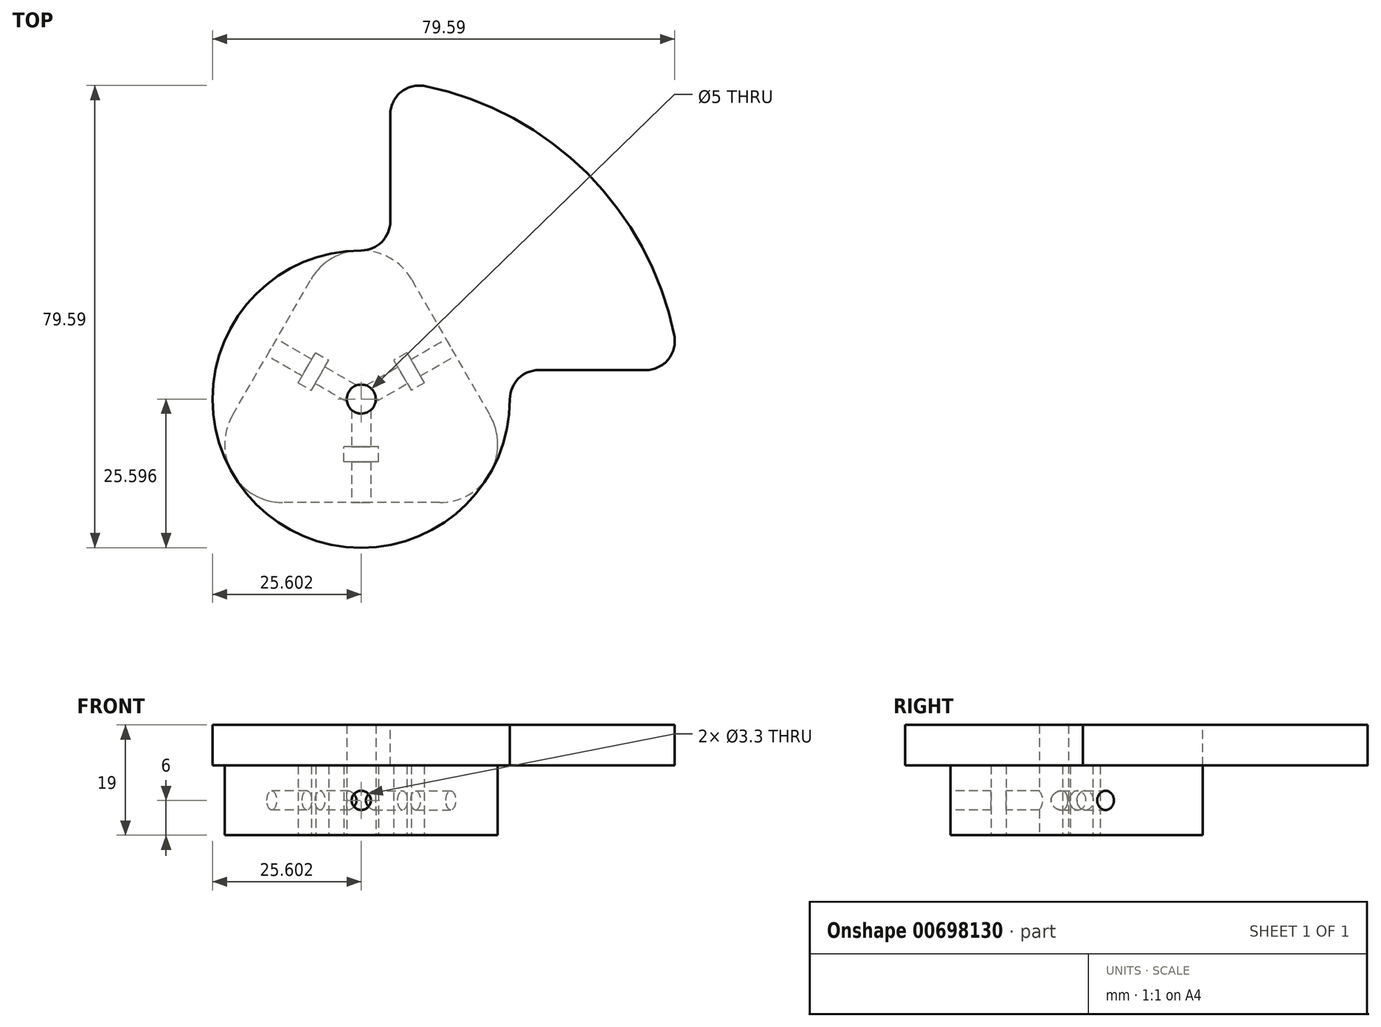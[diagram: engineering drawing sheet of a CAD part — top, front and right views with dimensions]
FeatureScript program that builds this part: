
annotation { "Feature Type Name" : "Feature", "Feature Type Description" : "" }
export const myFeature = defineFeature(function(context is Context, id is Id, definition is map)
    precondition{}
    {
        {
            var Q0;
            Q0=qCreatedBy(makeId("Top.planeOp"),FACE);
            var sketch = newSketch(context, id + "F0", { "sketchPlane" : qUnion([Q0])});
            skCircle(sketch, "E0.cCircle", {"center": v(-16.65, 9.96) * mm, "radius": 35.6 * mm, "construction": true});
            skLineSegment(sketch, "E0.0", {"start": v(14.18, -7.84) * mm, "end": v(-47.48, -7.84) * mm});
            skLineSegment(sketch, "E0.1", {"start": v(-47.48, -7.84) * mm, "end": v(-16.65, 45.56) * mm});
            skLineSegment(sketch, "E0.2", {"start": v(-16.65, 45.56) * mm, "end": v(14.18, -7.84) * mm});
            skCircle(sketch, "E1", {"center": v(-16.65, 9.96) * mm, "radius": 2.5 * mm});
            skPoint(sketch, "E2", {"position": v(-32.06, 18.86) * mm});
            skPoint(sketch, "E3", {"position": v(-1.23, 18.86) * mm});
            skPoint(sketch, "E4", {"position": v(-16.65, -7.84) * mm});
            skLineSegment(sketch, "E5", {"start": v(-32.06, 18.86) * mm, "end": v(-16.65, 9.96) * mm, "construction": true});
            skLineSegment(sketch, "E6", {"start": v(-16.65, -7.84) * mm, "end": v(-16.65, 9.96) * mm, "construction": true});
            skLineSegment(sketch, "E7", {"start": v(-16.65, 9.96) * mm, "end": v(-1.23, 18.86) * mm, "construction": true});
            skLineSegment(sketch, "E8.bottom", {"start": v(-13.65, -0.84) * mm, "end": v(-19.65, -0.84) * mm});
            skLineSegment(sketch, "E8.top", {"start": v(-13.65, 1.76) * mm, "end": v(-19.65, 1.76) * mm});
            skLineSegment(sketch, "E8.left", {"start": v(-13.65, -0.84) * mm, "end": v(-13.65, 1.76) * mm});
            skLineSegment(sketch, "E8.right", {"start": v(-19.65, -0.84) * mm, "end": v(-19.65, 1.76) * mm});
            skPoint(sketch, "E8.middle", {"position": v(-16.65, 0.46) * mm});
            skLineSegment(sketch, "E9.1.0", {"start": v(-8.8, 17.95) * mm, "end": v(-5.8, 12.76) * mm});
            skLineSegment(sketch, "E9.1.1", {"start": v(-11.05, 16.65) * mm, "end": v(-8.05, 11.46) * mm});
            skLineSegment(sketch, "E9.1.2", {"start": v(-8.8, 17.95) * mm, "end": v(-11.05, 16.65) * mm});
            skLineSegment(sketch, "E9.1.3", {"start": v(-5.8, 12.76) * mm, "end": v(-8.05, 11.46) * mm});
            skPoint(sketch, "E9.1.4", {"position": v(-8.42, 14.7) * mm});
            skLineSegment(sketch, "E9.2.0", {"start": v(-27.5, 12.76) * mm, "end": v(-24.5, 17.95) * mm});
            skLineSegment(sketch, "E9.2.1", {"start": v(-25.25, 11.46) * mm, "end": v(-22.25, 16.65) * mm});
            skLineSegment(sketch, "E9.2.2", {"start": v(-27.5, 12.76) * mm, "end": v(-25.25, 11.46) * mm});
            skLineSegment(sketch, "E9.2.3", {"start": v(-24.5, 17.95) * mm, "end": v(-22.25, 16.65) * mm});
            skPoint(sketch, "E9.2.4", {"position": v(-24.88, 14.7) * mm});
            skSolve(sketch);
        }
        {
            var Q0;
            Q0=makeQuery(id+"F0.imprint","IMPRINT",FACE,{"disambiguationData":[TD([[makeQuery(id+"F0.imprint","IMPRINT",EDGE,{"derivedFrom":sQuery(id+"F0.wireOp",EDGE,"E0.0")}),-1.0]])]});
            var Q1;
            Q1=makeQuery(id+"F0.imprint","IMPRINT",FACE,{"disambiguationData":[TD([[makeQuery(id+"F0.imprint","IMPRINT",EDGE,{"derivedFrom":sQuery(id+"F0.wireOp",EDGE,"E8.bottom")}),-1.0]])]});
            var Q2;
            Q2=makeQuery(id+"F0.imprint","IMPRINT",FACE,{"disambiguationData":[TD([[makeQuery(id+"F0.imprint","IMPRINT",EDGE,{"derivedFrom":sQuery(id+"F0.wireOp",EDGE,"E9.1.0")}),-1.0]])]});
            var Q3;
            Q3=makeQuery(id+"F0.imprint","IMPRINT",FACE,{"disambiguationData":[TD([[makeQuery(id+"F0.imprint","IMPRINT",EDGE,{"derivedFrom":sQuery(id+"F0.wireOp",EDGE,"E9.2.0")}),-1.0]])]});
            extrude(context, id + "F1", {"entities" : qUnion([Q0, Q1, Q2, Q3]), "depth" : 12 * mm, "offsetDistance" : 25 * mm});
        }
        {
            var Q0;
            Q0=makeQuery(id+"F1.opExtrude","SWEPT_EDGE",EDGE,{"disambiguationData":[OSD([sQuery(id+"F0.wireOp",EDGE,"E0.0"),sQuery(id+"F0.wireOp",EDGE,"E0.1")])]});
            var Q1;
            Q1=makeQuery(id+"F1.opExtrude","SWEPT_EDGE",EDGE,{"disambiguationData":[OSD([sQuery(id+"F0.wireOp",EDGE,"E0.0"),sQuery(id+"F0.wireOp",EDGE,"E0.2")])]});
            var Q2;
            Q2=makeQuery(id+"F1.opExtrude","SWEPT_EDGE",EDGE,{"disambiguationData":[OSD([sQuery(id+"F0.wireOp",EDGE,"E0.1"),sQuery(id+"F0.wireOp",EDGE,"E0.2")])]});
            fillet(context, id + "F2", {"entities" : qUnion([Q0, Q1, Q2]), "radius" : 10 * mm, "tangentPropagation" : true, "allowEdgeOverflow" : false});
        }
        {
            var Q0;
            Q0=makeQuery(id+"F0.imprint","IMPRINT",FACE,{"disambiguationData":[TD([[makeQuery(id+"F0.imprint","IMPRINT",EDGE,{"derivedFrom":sQuery(id+"F0.wireOp",EDGE,"E9.2.0")}),-1.0]])]});
            var Q1;
            Q1=makeQuery(id+"F0.imprint","IMPRINT",FACE,{"disambiguationData":[TD([[makeQuery(id+"F0.imprint","IMPRINT",EDGE,{"derivedFrom":sQuery(id+"F0.wireOp",EDGE,"E9.1.0")}),-1.0]])]});
            var Q2;
            Q2=makeQuery(id+"F0.imprint","IMPRINT",FACE,{"disambiguationData":[TD([[makeQuery(id+"F0.imprint","IMPRINT",EDGE,{"derivedFrom":sQuery(id+"F0.wireOp",EDGE,"E8.bottom")}),-1.0]])]});
            extrude(context, id + "F3", {"entities" : qUnion([Q0, Q1, Q2]), "operationType" : NewBodyOperationType.REMOVE, "depth" : 12 * mm, "offsetDistance" : 25 * mm});
        }
        {
            var Q0;
            Q0=makeQuery(id+"F1.opExtrude","CAP_FACE",FACE,{"disambiguationData":[OSD([sQuery(id+"F0.wireOp",EDGE,"E0.0"),sQuery(id+"F0.wireOp",EDGE,"E0.1"),sQuery(id+"F0.wireOp",EDGE,"E0.2"),sQuery(id+"F0.wireOp",EDGE,"E1")])],"isStart":false});
            var sketch = newSketch(context, id + "F4", { "sketchPlane" : qUnion([Q0])});
            skCircle(sketch, "E10.0", {"center": v(-16.65, 9.96) * mm, "radius": 2.5 * mm});
            skCircle(sketch, "E11", {"center": v(-16.65, 9.96) * mm, "radius": 60 * mm});
            skSolve(sketch);
        }
        {
            var Q0;
            Q0 = qSketchRegion(id + "F4", true);
            extrude(context, id + "F5", {"entities" : qUnion([Q0]), "operationType" : NewBodyOperationType.ADD, "depth" : 7 * mm, "offsetDistance" : 25 * mm});
        }
        {
            var Q0;
            Q0=makeQuery(id+"F5.opExtrude","CAP_FACE",FACE,{"disambiguationData":[OSD([sQuery(id+"F4.wireOp",EDGE,"E10.0"),sQuery(id+"F4.wireOp",EDGE,"E11")])],"isStart":false});
            var sketch = newSketch(context, id + "F6", { "sketchPlane" : qUnion([Q0])});
            skCircle(sketch, "E12.0", {"center": v(-16.65, 9.96) * mm, "radius": 60 * mm});
            skCircle(sketch, "E12.1", {"center": v(-16.65, 9.96) * mm, "radius": 2.5 * mm});
            skLineSegment(sketch, "E13", {"start": v(39.56, 75.26) * mm, "end": v(36.71, 73.2) * mm, "construction": true});
            skLineSegment(sketch, "E14", {"start": v(-16.65, 69.96) * mm, "end": v(-16.65, 9.96) * mm, "construction": true});
            skPoint(sketch, "E15", {"position": v(-16.65, 59.96) * mm});
            skPoint(sketch, "E16.1.0", {"position": v(-66.65, 9.96) * mm});
            skPoint(sketch, "E16.2.0", {"position": v(-16.65, -40.04) * mm});
            skPoint(sketch, "E16.3.0", {"position": v(33.35, 9.96) * mm});
            skArc(sketch, "E17", {"start": v(-11.65, 64.73) * mm, "mid": v(22.24, 48.85) * mm, "end": v(38.12, 14.96) * mm});
            skLineSegment(sketch, "E18.0.0", {"start": v(-38.82, 7.16) * mm, "end": v(-25.3, 30.56) * mm});
            skArc(sketch, "E18.0.1", {"start": v(-25.3, 30.56) * mm, "mid": v(-16.65, 35.56) * mm, "end": v(-7.99, 30.56) * mm});
            skLineSegment(sketch, "E18.0.2", {"start": v(-7.99, 30.56) * mm, "end": v(5.52, 7.16) * mm});
            skArc(sketch, "E18.0.3", {"start": v(5.52, 7.16) * mm, "mid": v(5.52, -2.84) * mm, "end": v(-3.14, -7.84) * mm});
            skLineSegment(sketch, "E18.0.4", {"start": v(-3.14, -7.84) * mm, "end": v(-30.16, -7.84) * mm});
            skArc(sketch, "E18.0.5", {"start": v(-30.16, -7.84) * mm, "mid": v(-38.82, -2.84) * mm, "end": v(-38.82, 7.16) * mm});
            skCircle(sketch, "E19", {"center": v(-16.65, 9.96) * mm, "radius": 22.35 * mm});
            skCircle(sketch, "E20", {"center": v(-16.65, 9.96) * mm, "radius": 25.6 * mm});
            skLineSegment(sketch, "E21", {"start": v(38.12, 14.96) * mm, "end": v(8.46, 14.96) * mm});
            skLineSegment(sketch, "E22", {"start": v(-11.65, 64.73) * mm, "end": v(-11.65, 35.06) * mm});
            skLineSegment(sketch, "E23.1.0", {"start": v(-71.42, 14.96) * mm, "end": v(-41.76, 14.96) * mm});
            skArc(sketch, "E23.1.1", {"start": v(-71.42, 14.96) * mm, "mid": v(-55.54, 48.85) * mm, "end": v(-21.65, 64.73) * mm});
            skLineSegment(sketch, "E23.1.2", {"start": v(-21.65, 64.73) * mm, "end": v(-21.65, 35.06) * mm});
            skLineSegment(sketch, "E23.2.0", {"start": v(-21.65, -44.82) * mm, "end": v(-21.65, -15.15) * mm});
            skArc(sketch, "E23.2.1", {"start": v(-21.65, -44.82) * mm, "mid": v(-55.54, -28.93) * mm, "end": v(-71.42, 4.96) * mm});
            skLineSegment(sketch, "E23.2.2", {"start": v(-71.42, 4.96) * mm, "end": v(-41.76, 4.96) * mm});
            skLineSegment(sketch, "E23.3.0", {"start": v(38.12, 4.96) * mm, "end": v(8.46, 4.96) * mm});
            skArc(sketch, "E23.3.1", {"start": v(38.12, 4.96) * mm, "mid": v(22.24, -28.93) * mm, "end": v(-11.65, -44.82) * mm});
            skLineSegment(sketch, "E23.3.2", {"start": v(-11.65, -44.82) * mm, "end": v(-11.65, -15.15) * mm});
            skSolve(sketch);
        }
        {
            var Q0;
            {var subQ0=sQuery(id+"F6.wireOp",EDGE,"E23.1.0");Q0=makeQuery(id+"F6.imprint","IMPRINT",FACE,{"disambiguationData":[TD([[makeQuery(id+"F6.imprint","IMPRINT",EDGE,{"derivedFrom":subQ0}),1.0]])]});}
            var Q1;
            Q1=makeQuery(id+"F6.imprint","IMPRINT",FACE,{"disambiguationData":[TD([[makeQuery(id+"F6.imprint","IMPRINT",EDGE,{"derivedFrom":sQuery(id+"F6.wireOp",EDGE,"E17")}),-1.0]])]});
            var Q2;
            {var subQ0=sQuery(id+"F6.wireOp",EDGE,"E23.3.0");Q2=makeQuery(id+"F6.imprint","IMPRINT",FACE,{"disambiguationData":[TD([[makeQuery(id+"F6.imprint","IMPRINT",EDGE,{"derivedFrom":subQ0}),1.0]])]});}
            var Q3;
            {var subQ0=sQuery(id+"F6.wireOp",EDGE,"E23.2.0");Q3=makeQuery(id+"F6.imprint","IMPRINT",FACE,{"disambiguationData":[TD([[makeQuery(id+"F6.imprint","IMPRINT",EDGE,{"derivedFrom":subQ0}),1.0]])]});}
            extrude(context, id + "F7", {"entities" : qUnion([Q0, Q1, Q2, Q3]), "operationType" : NewBodyOperationType.REMOVE, "oppositeDirection" : true, "depth" : 25 * mm, "offsetDistance" : 25 * mm});
        }
        {
            var Q0;
            Q0=sQuery(id+"F6.wireOp",VERTEX,"E16.1.0");
            var Q1;
            Q1=sQuery(id+"F6.wireOp",VERTEX,"E15");
            var Q2;
            Q2=sQuery(id+"F6.wireOp",VERTEX,"E16.3.0");
            var Q3;
            Q3=sQuery(id+"F6.wireOp",VERTEX,"E16.2.0");
            var Q4;
            Q4=makeQuery(id+"F1.opExtrude","SWEPT_BODY",BODY,{"disambiguationData":[OSD([sQuery(id+"F0.wireOp",EDGE,"E0.0"),sQuery(id+"F0.wireOp",EDGE,"E0.1"),sQuery(id+"F0.wireOp",EDGE,"E0.2"),sQuery(id+"F0.wireOp",EDGE,"E1")])]});
            hole(context, id + "F8", {"style" : HoleStyle.SIMPLE, "endStyle" : HoleEndStyle.BLIND, "standardTappedOrClearance" : lookupTablePath({ "standard" : "ISO", "fit" : "Normal", "size" : "M3", "type" : "Clearance" }), "standardBlindInLast" : lookupTablePath({ "fit" : "Standard", "standard" : "ISO", "size" : "M3", "type" : "Clearance" }), "holeDiameter" : 3.3 * mm, "majorDiameter" : 5 * mm, "holeDepth" : 20 * mm, "isTappedThrough" : true, "tappedDepth" : 12 * mm, "tapClearance" : 3, "startFromSketch" : true, "locations" : qUnion([Q0, Q1, Q2, Q3]), "scope" : qUnion([Q4])});
        }
        {
            var Q0;
            Q0=makeQuery(id+"F7.boolean.opBoolean","COPY",EDGE,{"derivedFrom":makeQuery(id+"F7.opExtrude","SWEPT_EDGE",EDGE,{"disambiguationData":[OSD([sQuery(id+"F6.wireOp",EDGE,"E20"),sQuery(id+"F6.wireOp",EDGE,"E23.2.2")])]})});
            var Q1;
            Q1=makeQuery(id+"F7.boolean.opBoolean","COPY",EDGE,{"derivedFrom":makeQuery(id+"F7.opExtrude","SWEPT_EDGE",EDGE,{"disambiguationData":[OSD([sQuery(id+"F6.wireOp",EDGE,"E20"),sQuery(id+"F6.wireOp",EDGE,"E23.1.0")])]})});
            var Q2;
            Q2=makeQuery(id+"F7.boolean.opBoolean","COPY",EDGE,{"derivedFrom":makeQuery(id+"F7.opExtrude","SWEPT_EDGE",EDGE,{"disambiguationData":[OSD([sQuery(id+"F6.wireOp",EDGE,"E20"),sQuery(id+"F6.wireOp",EDGE,"E23.1.2")])]})});
            var Q3;
            Q3=makeQuery(id+"F7.boolean.opBoolean","COPY",EDGE,{"derivedFrom":makeQuery(id+"F7.opExtrude","SWEPT_EDGE",EDGE,{"disambiguationData":[OSD([sQuery(id+"F6.wireOp",EDGE,"E20"),sQuery(id+"F6.wireOp",EDGE,"E22")])]})});
            var Q4;
            Q4=makeQuery(id+"F7.boolean.opBoolean","COPY",EDGE,{"derivedFrom":makeQuery(id+"F7.opExtrude","SWEPT_EDGE",EDGE,{"disambiguationData":[OSD([sQuery(id+"F6.wireOp",EDGE,"E20"),sQuery(id+"F6.wireOp",EDGE,"E21")])]})});
            var Q5;
            Q5=makeQuery(id+"F7.boolean.opBoolean","COPY",EDGE,{"derivedFrom":makeQuery(id+"F7.opExtrude","SWEPT_EDGE",EDGE,{"disambiguationData":[OSD([sQuery(id+"F6.wireOp",EDGE,"E20"),sQuery(id+"F6.wireOp",EDGE,"E23.3.0")])]})});
            var Q6;
            Q6=makeQuery(id+"F7.boolean.opBoolean","COPY",EDGE,{"derivedFrom":makeQuery(id+"F7.opExtrude","SWEPT_EDGE",EDGE,{"disambiguationData":[OSD([sQuery(id+"F6.wireOp",EDGE,"E20"),sQuery(id+"F6.wireOp",EDGE,"E23.3.2")])]})});
            var Q7;
            Q7=makeQuery(id+"F7.boolean.opBoolean","COPY",EDGE,{"derivedFrom":makeQuery(id+"F7.opExtrude","SWEPT_EDGE",EDGE,{"disambiguationData":[OSD([sQuery(id+"F6.wireOp",EDGE,"E20"),sQuery(id+"F6.wireOp",EDGE,"E23.2.0")])]})});
            var Q8;
            Q8=makeQuery(id+"F7.boolean.opBoolean","COPY",EDGE,{"derivedFrom":makeQuery(id+"F7.opExtrude","SWEPT_EDGE",EDGE,{"disambiguationData":[OSD([sQuery(id+"F6.wireOp",EDGE,"E17"),sQuery(id+"F6.wireOp",EDGE,"E21")])]})});
            var Q9;
            Q9=makeQuery(id+"F7.boolean.opBoolean","COPY",EDGE,{"derivedFrom":makeQuery(id+"F7.opExtrude","SWEPT_EDGE",EDGE,{"disambiguationData":[OSD([sQuery(id+"F6.wireOp",EDGE,"E17"),sQuery(id+"F6.wireOp",EDGE,"E22")])]})});
            var Q10;
            Q10=makeQuery(id+"F7.boolean.opBoolean","COPY",EDGE,{"derivedFrom":makeQuery(id+"F7.opExtrude","SWEPT_EDGE",EDGE,{"disambiguationData":[OSD([sQuery(id+"F6.wireOp",EDGE,"E23.1.1"),sQuery(id+"F6.wireOp",EDGE,"E23.1.2")])]})});
            var Q11;
            Q11=makeQuery(id+"F7.boolean.opBoolean","COPY",EDGE,{"derivedFrom":makeQuery(id+"F7.opExtrude","SWEPT_EDGE",EDGE,{"disambiguationData":[OSD([sQuery(id+"F6.wireOp",EDGE,"E23.1.0"),sQuery(id+"F6.wireOp",EDGE,"E23.1.1")])]})});
            var Q12;
            Q12=makeQuery(id+"F7.boolean.opBoolean","COPY",EDGE,{"derivedFrom":makeQuery(id+"F7.opExtrude","SWEPT_EDGE",EDGE,{"disambiguationData":[OSD([sQuery(id+"F6.wireOp",EDGE,"E23.2.1"),sQuery(id+"F6.wireOp",EDGE,"E23.2.2")])]})});
            var Q13;
            Q13=makeQuery(id+"F7.boolean.opBoolean","COPY",EDGE,{"derivedFrom":makeQuery(id+"F7.opExtrude","SWEPT_EDGE",EDGE,{"disambiguationData":[OSD([sQuery(id+"F6.wireOp",EDGE,"E23.2.0"),sQuery(id+"F6.wireOp",EDGE,"E23.2.1")])]})});
            var Q14;
            Q14=makeQuery(id+"F7.boolean.opBoolean","COPY",EDGE,{"derivedFrom":makeQuery(id+"F7.opExtrude","SWEPT_EDGE",EDGE,{"disambiguationData":[OSD([sQuery(id+"F6.wireOp",EDGE,"E23.3.1"),sQuery(id+"F6.wireOp",EDGE,"E23.3.2")])]})});
            var Q15;
            Q15=makeQuery(id+"F7.boolean.opBoolean","COPY",EDGE,{"derivedFrom":makeQuery(id+"F7.opExtrude","SWEPT_EDGE",EDGE,{"disambiguationData":[OSD([sQuery(id+"F6.wireOp",EDGE,"E23.3.0"),sQuery(id+"F6.wireOp",EDGE,"E23.3.1")])]})});
            fillet(context, id + "F9", {"entities" : qUnion([Q0, Q1, Q2, Q3, Q4, Q5, Q6, Q7, Q8, Q9, Q10, Q11, Q12, Q13, Q14, Q15]), "radius" : 5 * mm, "tangentPropagation" : true, "allowEdgeOverflow" : false});
        }
        {
            var Q0;
            Q0=makeQuery(id+"F1.opExtrude","SWEPT_FACE",FACE,{"disambiguationData":[OSD([sQuery(id+"F0.wireOp",EDGE,"E0.0")])]});
            var sketch = newSketch(context, id + "F10", { "sketchPlane" : qUnion([Q0])});
            skPoint(sketch, "E24", {"position": v(-16.65, 6) * mm});
            skPoint(sketch, "E24.positionSnap0", {"position": v(-16.65, 12) * mm});
            skPoint(sketch, "E24.positionSnap1", {"position": v(-30.16, 6) * mm});
            skSolve(sketch);
        }
        {
            var Q0;
            Q0=makeQuery(id+"F1.opExtrude","SWEPT_FACE",FACE,{"disambiguationData":[OSD([sQuery(id+"F0.wireOp",EDGE,"E0.2")])]});
            var sketch = newSketch(context, id + "F11", { "sketchPlane" : qUnion([Q0])});
            skPoint(sketch, "E25", {"position": v(16.95, 6) * mm});
            skPoint(sketch, "E25.positionSnap0", {"position": v(16.95, 12) * mm});
            skPoint(sketch, "E25.positionSnap1", {"position": v(3.44, 6) * mm});
            skSolve(sketch);
        }
        {
            var Q0;
            Q0=makeQuery(id+"F1.opExtrude","SWEPT_FACE",FACE,{"disambiguationData":[OSD([sQuery(id+"F0.wireOp",EDGE,"E0.1")])]});
            var sketch = newSketch(context, id + "F12", { "sketchPlane" : qUnion([Q0])});
            skPoint(sketch, "E26", {"position": v(-0.3, 6) * mm});
            skPoint(sketch, "E26.positionSnap0", {"position": v(-0.3, 12) * mm});
            skPoint(sketch, "E26.positionSnap1", {"position": v(-13.8, 6) * mm});
            skSolve(sketch);
        }
        {
            var Q0;
            Q0=sQuery(id+"F12.wireOp",VERTEX,"E26");
            var Q1;
            Q1=sQuery(id+"F10.wireOp",VERTEX,"E24");
            var Q2;
            Q2=sQuery(id+"F11.wireOp",VERTEX,"E25");
            var Q3;
            Q3=makeQuery(id+"F1.opExtrude","SWEPT_BODY",BODY,{"disambiguationData":[OSD([sQuery(id+"F0.wireOp",EDGE,"E0.0"),sQuery(id+"F0.wireOp",EDGE,"E0.1"),sQuery(id+"F0.wireOp",EDGE,"E0.2"),sQuery(id+"F0.wireOp",EDGE,"E1")])]});
            hole(context, id + "F13", {"style" : HoleStyle.SIMPLE, "endStyle" : HoleEndStyle.BLIND, "standardTappedOrClearance" : lookupTablePath({ "standard" : "ISO", "fit" : "Normal", "size" : "M3", "type" : "Clearance" }), "standardBlindInLast" : lookupTablePath({ "fit" : "Standard", "standard" : "ISO", "size" : "M3", "type" : "Clearance" }), "holeDiameter" : 3.3 * mm, "majorDiameter" : 5 * mm, "holeDepth" : 17 * mm, "isTappedThrough" : true, "tappedDepth" : 12 * mm, "tapClearance" : 3, "startFromSketch" : true, "locations" : qUnion([Q0, Q1, Q2]), "scope" : qUnion([Q3])});
        }
    });
